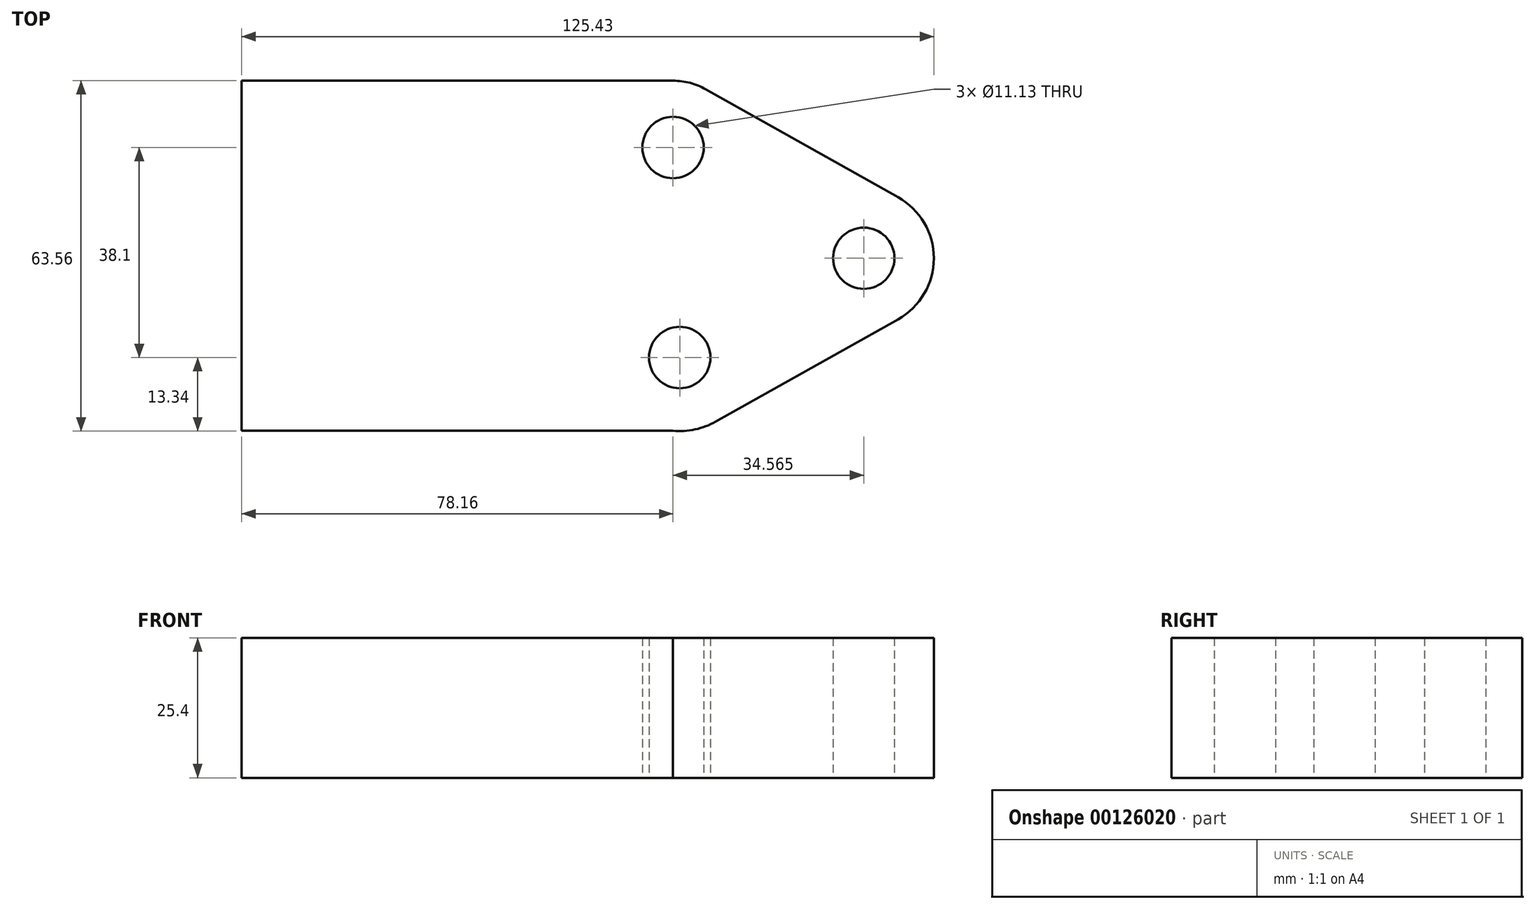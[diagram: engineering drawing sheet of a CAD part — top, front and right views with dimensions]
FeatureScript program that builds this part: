
annotation { "Feature Type Name" : "Feature", "Feature Type Description" : "" }
export const myFeature = defineFeature(function(context is Context, id is Id, definition is map)
    precondition{}
    {
        {
            var Q0;
            Q0=qCreatedBy(makeId("Top.planeOp"),FACE);
            var sketch = newSketch(context, id + "F0", { "sketchPlane" : qUnion([Q0])});
            skLineSegment(sketch, "E0", {"start": v(0, 63.5) * mm, "end": v(0, 0) * mm});
            skLineSegment(sketch, "E1", {"start": v(0, 0) * mm, "end": v(78.16, 0) * mm});
            skLineSegment(sketch, "E2", {"start": v(0, 63.5) * mm, "end": v(78.16, 63.5) * mm});
            skLineSegment(sketch, "E3", {"start": v(66.04, 51.38) * mm, "end": v(66.04, 13.28) * mm});
            skArc(sketch, "E4", {"start": v(66.04, 51.38) * mm, "mid": v(72.04, 61.84) * mm, "end": v(84.1, 61.95) * mm});
            skArc(sketch, "E5", {"start": v(66.04, 13.28) * mm, "mid": v(72.64, 1.77) * mm, "end": v(85.9, 1.65) * mm});
            skLineSegment(sketch, "E6", {"start": v(84.1, 61.95) * mm, "end": v(118.95, 42.36) * mm});
            skLineSegment(sketch, "E7", {"start": v(85.9, 1.65) * mm, "end": v(118.95, 20.22) * mm});
            skArc(sketch, "E8", {"start": v(118.95, 42.36) * mm, "mid": v(125.43, 31.3) * mm, "end": v(118.95, 20.22) * mm});
            skCircle(sketch, "E9", {"center": v(78.16, 51.38) * mm, "radius": 5.56 * mm});
            skCircle(sketch, "E10", {"center": v(112.73, 31.3) * mm, "radius": 5.56 * mm});
            skCircle(sketch, "E11", {"center": v(79.38, 13.28) * mm, "radius": 5.56 * mm});
            skLineSegment(sketch, "E12", {"start": v(28.58, 73.3) * mm, "end": v(28.58, -13.38) * mm, "construction": true});
            skSolve(sketch);
        }
        {
            var Q0;
            Q0 = qSketchRegion(id + "F0", true);
            extrude(context, id + "F1", {"entities" : qUnion([Q0]), "depth" : 25.4 * mm});
        }
    });
